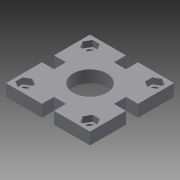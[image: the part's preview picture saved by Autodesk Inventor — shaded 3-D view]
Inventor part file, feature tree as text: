
AUTODESK INVENTOR PART (.ipt)
format: ipt  version: 2015 (Build 190159000, 159)  size: 187,904 bytes
history: native  units: mm
features: extrude x4, sketch x4, pattern_circular x2
ambient origin geometry x8: Origin, YZ Plane, XZ Plane, XY Plane, X Axis, Y Axis, Z Axis, Center Point
bodies: Solid1 (feature_tree)
feature tree (10):
  extrude  "Extrusion1"  Depth=2.5mm
  extrude  "Extrusion4"  Depth=5.0mm
  extrude  "Extrusion5"  Depth=5.0mm
  pattern_circular  "Circular Pattern2"  [2 undecoded]
  extrude  "Extrusion6"  Depth=5.0mm
  pattern_circular  "Circular Pattern4"  [2 undecoded]
  sketch  "Sketch1"  dims[d0=5.0mm d1=2.5mm]
  sketch  "Sketch4"  dims[d2=5.0mm d3=5.0mm]
  sketch  "Sketch5"  dims[d4=5.0mm d5=5.0mm]
  sketch  "Sketch6"  dims[d6=5.0mm d7=2.5mm d8=5.0mm d9=5.0mm d10=5.0mm d11=5.0mm d12=5.0mm d13=5.0mm d14=5.0mm d15=5.0mm d16=5.0mm d17=5.0mm d18=5.0mm d19=5.0mm d20=5.0mm d21=5.0mm d22=5.0mm d23=5.0mm d24=5.0mm d25=5.0mm d26=5.0mm d27=5.0mm d28=5.0mm d29=5.0mm d30=5.0mm d31=5.0mm d32=5.0mm d33=5.0mm d34=0.0mm d54=4.0mm d55=4.0mm d56=3.5mm d57=10.0mm d58=0.0mm d59=3.0mm d60=3.0mm d61=60.0deg d62=2.5mm d63=0.0mm d64=60.0mm d65=360.0deg d70=14.0mm d71=10.0mm d72=0.0mm d73=40.0mm d74=360.0deg]
note: 4 required parameter values undecoded (feature->parameter linkage not recoverable at this tier; creation-order binding heuristic only, values carry confidence <= 0.55)
